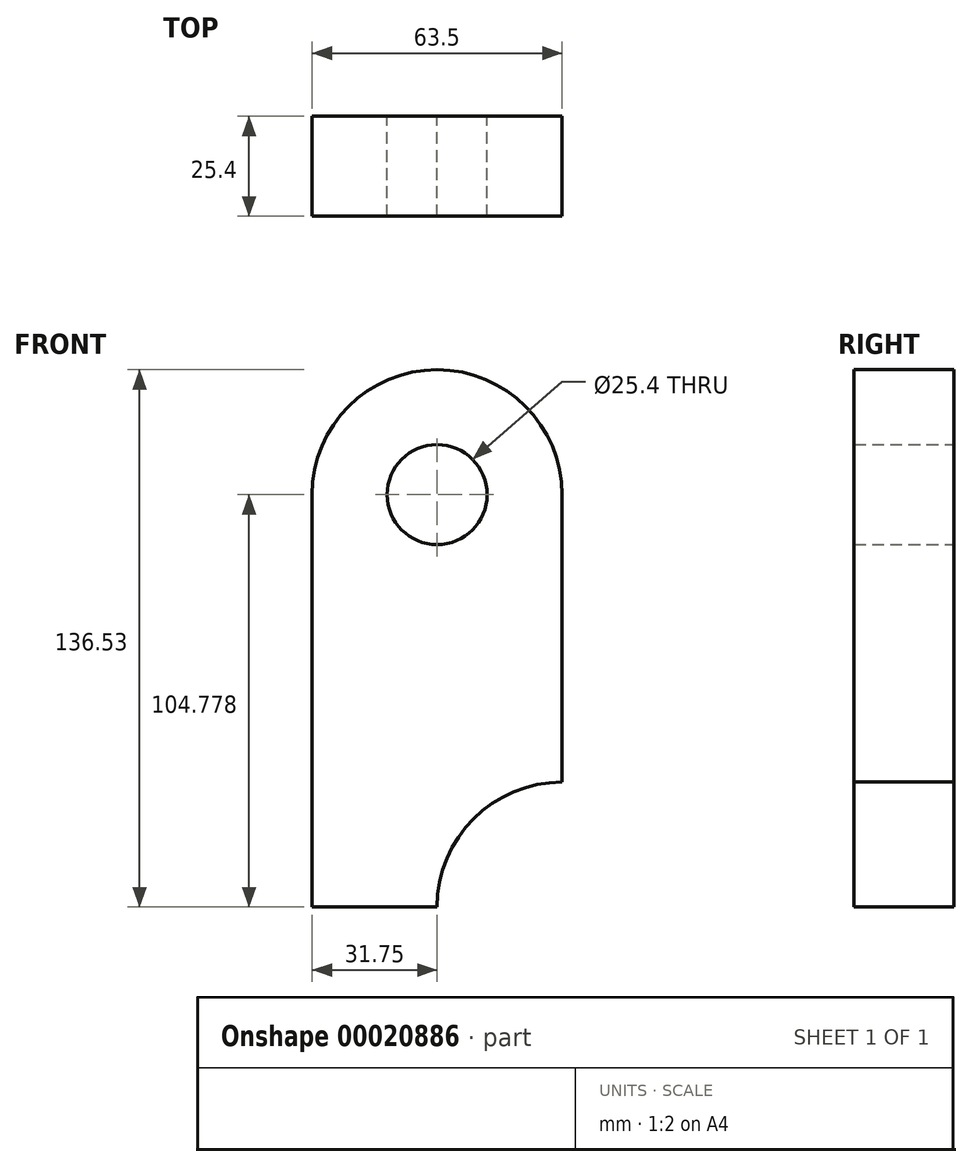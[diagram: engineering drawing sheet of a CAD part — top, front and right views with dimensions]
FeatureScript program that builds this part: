
annotation { "Feature Type Name" : "Feature", "Feature Type Description" : "" }
export const myFeature = defineFeature(function(context is Context, id is Id, definition is map)
    precondition{}
    {
        {
            var Q0;
            Q0=qCreatedBy(makeId("Front.planeOp"),FACE);
            var sketch = newSketch(context, id + "F0", { "sketchPlane" : qUnion([Q0])});
            skLineSegment(sketch, "E0.rect.top", {"start": v(0, -52.39) * mm, "end": v(-31.75, -52.39) * mm});
            skLineSegment(sketch, "E0.rect.left", {"start": v(31.75, 52.39) * mm, "end": v(31.75, -20.64) * mm});
            skLineSegment(sketch, "E0.rect.right", {"start": v(-31.75, 52.39) * mm, "end": v(-31.75, -52.39) * mm});
            skPoint(sketch, "E0.rect.middle", {"position": v(0, 0) * mm});
            skArc(sketch, "E1", {"start": v(31.75, 52.39) * mm, "mid": v(0, 84.14) * mm, "end": v(-31.75, 52.39) * mm});
            skCircle(sketch, "E2", {"center": v(0, 52.39) * mm, "radius": 12.7 * mm});
            skArc(sketch, "E3", {"start": v(31.75, -20.64) * mm, "mid": v(9.3, -29.94) * mm, "end": v(0, -52.39) * mm});
            skSolve(sketch);
        }
        {
            var Q0;
            Q0=makeQuery(id+"F0.imprint","IMPRINT",FACE,{"disambiguationData":[TD([[makeQuery(id+"F0.imprint","IMPRINT",EDGE,{"derivedFrom":sQuery(id+"F0.wireOp",EDGE,"E0.rect.top")}),-1.0]])]});
            extrude(context, id + "F1", {"entities" : qUnion([Q0]), "depth" : 25.4 * mm});
        }
    });
